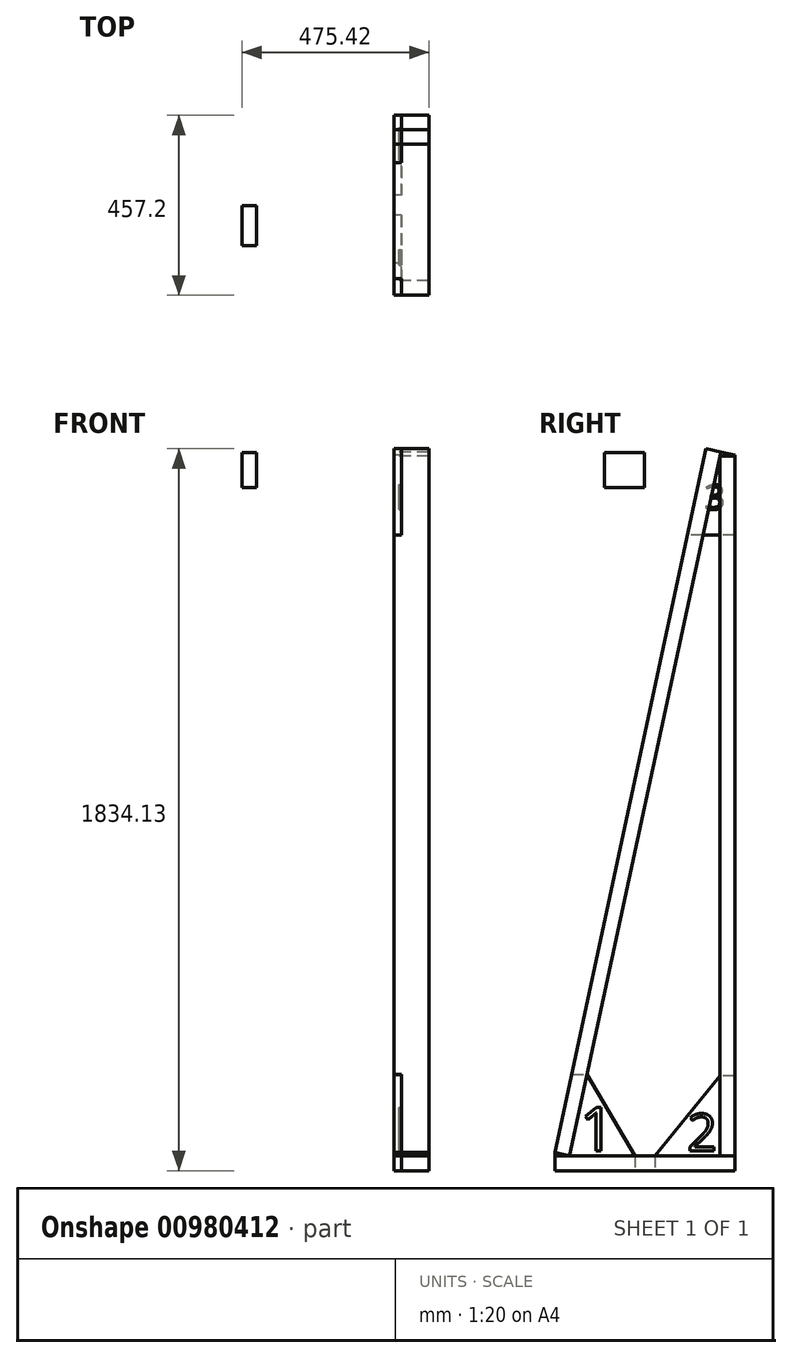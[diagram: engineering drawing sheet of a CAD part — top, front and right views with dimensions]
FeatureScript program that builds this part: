
annotation { "Feature Type Name" : "Feature", "Feature Type Description" : "" }
export const myFeature = defineFeature(function(context is Context, id is Id, definition is map)
    precondition{}
    {
        {
            var Q0;
            Q0=qCreatedBy(makeId("Right.planeOp"),FACE);
            var sketch = newSketch(context, id + "F0", { "sketchPlane" : qUnion([Q0])});
            skLineSegment(sketch, "E0.bottom", {"start": v(-227.88, -2.41) * mm, "end": v(229.32, -2.41) * mm});
            skLineSegment(sketch, "E0.top", {"start": v(-227.88, -40.51) * mm, "end": v(229.32, -40.51) * mm});
            skLineSegment(sketch, "E0.left", {"start": v(-227.88, -2.41) * mm, "end": v(-227.88, -40.51) * mm});
            skLineSegment(sketch, "E0.right", {"start": v(229.32, -2.41) * mm, "end": v(229.32, -40.51) * mm});
            skSolve(sketch);
        }
        {
            var Q0;
            Q0=makeQuery(id+"F0.imprint","IMPRINT",FACE,{"disambiguationData":[TD([[makeQuery(id+"F0.imprint","IMPRINT",EDGE,{"derivedFrom":sQuery(id+"F0.wireOp",EDGE,"E0.bottom")}),-1.0]])]});
            extrude(context, id + "F1", {"entities" : qUnion([Q0]), "depth" : 88.9 * mm, "offsetDistance" : 25.4 * mm});
        }
        {
            var Q0;
            Q0=qCreatedBy(makeId("Right.planeOp"),FACE);
            var sketch = newSketch(context, id + "F2", { "sketchPlane" : qUnion([Q0])});
            skLineSegment(sketch, "E1.bottom", {"start": v(191.22, 1775.59) * mm, "end": v(229.32, 1775.59) * mm});
            skLineSegment(sketch, "E1.top", {"start": v(191.22, -2.41) * mm, "end": v(229.32, -2.41) * mm});
            skLineSegment(sketch, "E1.left", {"start": v(191.22, 1775.59) * mm, "end": v(191.22, -2.41) * mm});
            skLineSegment(sketch, "E1.right", {"start": v(229.32, 1775.59) * mm, "end": v(229.32, -2.41) * mm});
            skSolve(sketch);
        }
        {
            var Q0;
            Q0=makeQuery(id+"F2.imprint","IMPRINT",FACE,{"disambiguationData":[TD([[makeQuery(id+"F2.imprint","IMPRINT",EDGE,{"derivedFrom":sQuery(id+"F2.wireOp",EDGE,"E1.bottom")}),-1.0]])]});
            extrude(context, id + "F3", {"entities" : qUnion([Q0]), "depth" : 88.9 * mm, "offsetDistance" : 25.4 * mm});
        }
        {
            var Q0;
            Q0=qCreatedBy(makeId("Right.planeOp"),FACE);
            var sketch = newSketch(context, id + "F4", { "sketchPlane" : qUnion([Q0])});
            skLineSegment(sketch, "E2", {"start": v(193.37, 1785.62) * mm, "end": v(156.12, 1793.62) * mm});
            skLineSegment(sketch, "E3", {"start": v(156.12, 1793.62) * mm, "end": v(-227.88, 5.59) * mm});
            skLineSegment(sketch, "E4", {"start": v(-227.88, 5.59) * mm, "end": v(-190.63, -2.41) * mm});
            skLineSegment(sketch, "E5", {"start": v(-190.63, -2.41) * mm, "end": v(193.37, 1785.62) * mm});
            skSolve(sketch);
        }
        {
            var Q0;
            Q0=makeQuery(id+"F4.imprint","IMPRINT",FACE,{"disambiguationData":[TD([[makeQuery(id+"F4.imprint","IMPRINT",EDGE,{"derivedFrom":sQuery(id+"F4.wireOp",EDGE,"E2")}),1.0]])]});
            extrude(context, id + "F5", {"entities" : qUnion([Q0]), "depth" : 88.9 * mm, "offsetDistance" : 25.4 * mm});
        }
        {
            var Q0;
            Q0=qCreatedBy(makeId("Right.planeOp"),FACE);
            var sketch = newSketch(context, id + "F6", { "sketchPlane" : qUnion([Q0])});
            skLineSegment(sketch, "E6", {"start": v(229.32, -40.51) * mm, "end": v(229.32, 200.79) * mm});
            skLineSegment(sketch, "E7", {"start": v(229.32, 200.79) * mm, "end": v(191.22, 200.79) * mm});
            skLineSegment(sketch, "E8", {"start": v(191.22, 200.79) * mm, "end": v(26.12, -2.41) * mm});
            skLineSegment(sketch, "E9", {"start": v(26.12, -2.41) * mm, "end": v(26.12, -40.51) * mm});
            skLineSegment(sketch, "E10", {"start": v(26.12, -40.51) * mm, "end": v(229.32, -40.51) * mm});
            skSolve(sketch);
        }
        {
            var Q0;
            Q0=makeQuery(id+"F6.imprint","IMPRINT",FACE,{"disambiguationData":[TD([[makeQuery(id+"F6.imprint","IMPRINT",EDGE,{"derivedFrom":sQuery(id+"F6.wireOp",EDGE,"E6")}),1.0]])]});
            extrude(context, id + "F7", {"entities" : qUnion([Q0]), "depth" : 19.05 * mm, "offsetDistance" : 25.4 * mm});
        }
        {
            var Q0;
            Q0=makeQuery(id+"F7.opExtrude","CAP_FACE",FACE,{"disambiguationData":[OSD([sQuery(id+"F6.wireOp",EDGE,"E6"),sQuery(id+"F6.wireOp",EDGE,"E7"),sQuery(id+"F6.wireOp",EDGE,"E8"),sQuery(id+"F6.wireOp",EDGE,"E9"),sQuery(id+"F6.wireOp",EDGE,"E10")])],"isStart":false});
            var sketch = newSketch(context, id + "F8", { "sketchPlane" : qUnion([Q0])});
            skText(sketch, "E11", { "text": "2", "fontName": "OpenSans-Regular.ttf"});
            const initialGuessF8  = {"E11": [0.10867, 0.01029, 1, 0, 0.09411]};
            skSetInitialGuess(sketch, initialGuessF8);
            skSolve(sketch);
        }
        {
            var Q0;
            Q0=makeQuery(id+"F8.imprint","IMPRINT",FACE,{"disambiguationData":[TD([[makeQuery(id+"F8.imprint","IMPRINT",EDGE,{"derivedFrom":sQuery(id+"F8.wireOp",EDGE,"E11.sketch_text.stroke-0")}),-1.0]])]});
            extrude(context, id + "F9", {"entities" : qUnion([Q0]), "operationType" : NewBodyOperationType.REMOVE, "oppositeDirection" : true, "depth" : 6.35 * mm, "offsetDistance" : 25.4 * mm});
        }
        {
            var Q0;
            Q0=qCreatedBy(makeId("Right.planeOp"),FACE);
            var sketch = newSketch(context, id + "F10", { "sketchPlane" : qUnion([Q0])});
            skLineSegment(sketch, "E12", {"start": v(-227.88, -40.51) * mm, "end": v(-227.88, 5.59) * mm});
            skLineSegment(sketch, "E13", {"start": v(-227.88, 5.59) * mm, "end": v(-185.21, 204.26) * mm});
            skLineSegment(sketch, "E14", {"start": v(-185.21, 204.26) * mm, "end": v(-146.25, 204.26) * mm});
            skLineSegment(sketch, "E15", {"start": v(-146.25, 204.26) * mm, "end": v(-24.68, -2.41) * mm});
            skLineSegment(sketch, "E16", {"start": v(-24.68, -2.41) * mm, "end": v(-24.68, -40.51) * mm});
            skLineSegment(sketch, "E17", {"start": v(-24.68, -40.51) * mm, "end": v(-227.88, -40.51) * mm});
            skSolve(sketch);
        }
        {
            var Q0;
            Q0=makeQuery(id+"F10.imprint","IMPRINT",FACE,{"disambiguationData":[TD([[makeQuery(id+"F10.imprint","IMPRINT",EDGE,{"derivedFrom":sQuery(id+"F10.wireOp",EDGE,"E12")}),-1.0]])]});
            extrude(context, id + "F11", {"entities" : qUnion([Q0]), "depth" : 19.05 * mm, "offsetDistance" : 25.4 * mm});
        }
        {
            var Q0;
            Q0=makeQuery(id+"F11.opExtrude","CAP_FACE",FACE,{"disambiguationData":[OSD([sQuery(id+"F10.wireOp",EDGE,"E12"),sQuery(id+"F10.wireOp",EDGE,"E13"),sQuery(id+"F10.wireOp",EDGE,"E14"),sQuery(id+"F10.wireOp",EDGE,"E15"),sQuery(id+"F10.wireOp",EDGE,"E16"),sQuery(id+"F10.wireOp",EDGE,"E17")])],"isStart":false});
            var sketch = newSketch(context, id + "F12", { "sketchPlane" : qUnion([Q0])});
            skText(sketch, "E18", { "text": "1", "fontName": "OpenSans-Regular.ttf"});
            skPoint(sketch, "E18.firstSnap0", {"position": v(-206.55, 104.92) * mm});
            const initialGuessF12  = {"E18": [-0.16487, 0.01029, 1, 0, 0.11046]};
            skSetInitialGuess(sketch, initialGuessF12);
            skSolve(sketch);
        }
        {
            var Q0;
            Q0=qSketchRegion(id+"F12",true);
            extrude(context, id + "F13", {"entities" : qUnion([Q0]), "operationType" : NewBodyOperationType.REMOVE, "oppositeDirection" : true, "depth" : 6.35 * mm, "offsetDistance" : 25.4 * mm});
        }
        {
            var Q0;
            Q0=qCreatedBy(makeId("Right.planeOp"),FACE);
            var sketch = newSketch(context, id + "F14", { "sketchPlane" : qUnion([Q0])});
            skLineSegment(sketch, "E19", {"start": v(109.1, 1574.7) * mm, "end": v(156.12, 1793.62) * mm});
            skLineSegment(sketch, "E20", {"start": v(156.12, 1793.62) * mm, "end": v(229.32, 1777.9) * mm});
            skLineSegment(sketch, "E21", {"start": v(229.32, 1777.9) * mm, "end": v(229.32, 1574.7) * mm});
            skLineSegment(sketch, "E22", {"start": v(229.32, 1574.7) * mm, "end": v(109.1, 1574.7) * mm});
            skSolve(sketch);
        }
        {
            var Q0;
            Q0=qSketchRegion(id+"F14",true);
            extrude(context, id + "F15", {"entities" : qUnion([Q0]), "depth" : 19.05 * mm, "offsetDistance" : 25.4 * mm});
        }
        {
            var Q0;
            Q0=makeQuery(id+"F15.opExtrude","CAP_FACE",FACE,{"disambiguationData":[OSD([sQuery(id+"F14.wireOp",EDGE,"E19"),sQuery(id+"F14.wireOp",EDGE,"E20"),sQuery(id+"F14.wireOp",EDGE,"E21"),sQuery(id+"F14.wireOp",EDGE,"E22")])],"isStart":false});
            var sketch = newSketch(context, id + "F16", { "sketchPlane" : qUnion([Q0])});
            skText(sketch, "E23", { "text": "3\n", "fontName": "OpenSans-Regular.ttf"});
            const initialGuessF16  = {"E23": [0.15312, 1.63955, 1, 0, 0.06328]};
            skSetInitialGuess(sketch, initialGuessF16);
            skSolve(sketch);
        }
        {
            var Q0;
            Q0=qSketchRegion(id+"F16",true);
            extrude(context, id + "F17", {"entities" : qUnion([Q0]), "operationType" : NewBodyOperationType.REMOVE, "oppositeDirection" : true, "depth" : 6.35 * mm, "offsetDistance" : 25.4 * mm});
        }
        {
            var Q0;
            Q0=qCreatedBy(makeId("Front.planeOp"),FACE);
            var sketch = newSketch(context, id + "F18", { "sketchPlane" : qUnion([Q0])});
            skLineSegment(sketch, "E24.bottom", {"start": v(-386.52, 1784.46) * mm, "end": v(-348.42, 1784.46) * mm});
            skLineSegment(sketch, "E24.top", {"start": v(-386.52, 1695.56) * mm, "end": v(-348.42, 1695.56) * mm});
            skLineSegment(sketch, "E24.left", {"start": v(-386.52, 1784.46) * mm, "end": v(-386.52, 1695.56) * mm});
            skLineSegment(sketch, "E24.right", {"start": v(-348.42, 1784.46) * mm, "end": v(-348.42, 1695.56) * mm});
            skSolve(sketch);
        }
        {
            var Q0;
            Q0=qSketchRegion(id+"F18",true);
            extrude(context, id + "F19", {"entities" : qUnion([Q0]), "depth" : 101.6 * mm, "offsetDistance" : 25.4 * mm});
        }
    });
